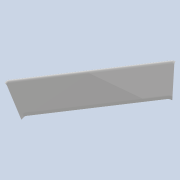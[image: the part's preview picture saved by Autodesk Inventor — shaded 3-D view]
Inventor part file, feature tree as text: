
AUTODESK INVENTOR PART (.ipt)
format: ipt  version: 2020.4 (Build 244396010, 396A)  size: 9,091,584 bytes
history: native  units: in
note: dims shown in document units (in); Inventor stores cm internally (conversion verified against a paired STEP export)
features: other x165, extrude x70, fillet x51, projected_geometry x6, sketch x5, move_body x5, hole x4, loft x3, plane x3, reference x2, boolean_combine x1, direct_edit x1, split x1
ambient origin geometry x8: Origin, YZ Plane, XZ Plane, XY Plane, X Axis, Y Axis, Z Axis, Center Point
bodies: Body (feature_tree), BodyFeature (feature_tree), BodyCut (feature_tree), BodyCutFeature (feature_tree), BodyCutFilletFeature (feature_tree), BodyCutCombineFeature (feature_tree), BodyCutEdgeFilletFeature (feature_tree), BodyRibFrontFilletsFeature (feature_tree), BodyBackRibFilletsFeature (feature_tree), BodyFretboardFilletsFeature (feature_tree), BodyFrontTopFilletsFeature (feature_tree), BodyFrontBottomFilletsFeature (feature_tree), BodyFrontNeckFilletsFeature (feature_tree), Solid22 (feature_tree), Solid23 (feature_tree), Solid62 (feature_tree), Solid64 (feature_tree), Solid65 (feature_tree), Solid68 (feature_tree), Solid50 (feature_tree), Solid52 (feature_tree), Solid54 (feature_tree), Solid56 (feature_tree), Solid57 (feature_tree), Solid59 (feature_tree)
feature tree (317):
  other  "MainBody"
  extrude  "NeckMountsProfileFeature"  Depth=0.5in TaperAngle=0.0deg
  other  "NeckPlane"
  extrude  "8StringFeature"  Depth=0.25in
  extrude  "6StringFeature"  Depth=0.25in
  extrude  "HornFeature"  Depth=0.25in
  other  "6StringNeckFeature"
  other  "8StringNeckFeature"
  fillet  "InsideCornerFilletsFeature1/8"  Radius=0.6788in
  fillet  "OutsideFilletsFeature1/2"  Radius=0.125in
  fillet  "NeckMountOutsideFilletsFeature1/4"  Radius=0.5in
  fillet  "TipFilletsFeature1/8"  Radius=0.125in
  fillet  "BottomHornTipFilletFeature1/10"  Radius=0.1in
  fillet  "BottomHornFilletsFeature1/8"  Radius=0.125in
  fillet  "InsideHandleFilletsFeature1/2"  Radius=0.5in
  fillet  "InsideHandleFilletsFeature1/8"  Radius=0.125in
  fillet  "InsideTopHornFilletsFeature1/4"  Radius=0.25in
  fillet  "InsideTopHornFilletsFeature1/2"  Radius=0.5in
  fillet  "InsideBottomHornFilletsFeature1/4"  Radius=0.25in
  other  "PickupsOriginal"
  other  "MiddlePlane"
  other  "PickupsCustom"
  other  "PickupsModified"
  extrude  "TopPickupsIndentFeature"  Depth=0.25in
  extrude  "BottomPickupsIndentFeature"  Depth=0.25in
  extrude  "TopPickupHolesFeature"  Depth=0.25in
  extrude  "BottomPickupHolesFeature"  Depth=0.25in
  fillet  "PickupIndentFilletsFeature"  Radius=1.1649in
  other  "Frets"
  other  "FretsPreview"
  other  "TopHornHandleIndent"
  extrude  "TopHornBodyHandleFeature"  Depth=0.25in
  extrude  "TopHornHornHandleFeature"  Depth=0.25in
  other  "HornSculptFeature"
  other  "TopHornHandleFront"
  extrude  "TopHornHandleFrontFeature"  Depth=0.25in
  extrude  "TopHornHandleFront2Feature"  Depth=0.25in
  extrude  "TopHornHandleFront3Feature"  TaperAngle=45.0deg  [1 undecoded]
  other  "TopHornHandleBack"
  extrude  "TopHornHandleBackFeature"  TaperAngle=120.0deg  [1 undecoded]
  extrude  "TopHornHandleBack2Feature"  Depth=0.25in
  extrude  "TopHandleFeature"  Depth=0.25in
  extrude  "TopHandleFrontFeature"  Depth=0.25in
  extrude  "TopHandleBackFeature"  Depth=0.25in
  other  "Tuners"
  hole  "TunerHolesFeature"  [1 undecoded]
  other  "LogoMount"
  extrude  "LogoMountFeature"  Depth=0.25in
  other  "SideProfile"
  extrude  "SideProfileFeature"  Depth=0.25in
  other  "KeyboardCompartmentSidePlane"
  extrude  "KeyboardCompartmentFeature"  Depth=0.25in
  fillet  "KeyboardCompartmentFilletsFeature"  Radius=0.101in
  other  "ControlsBottom"
  other  "ControlsTop2"
  other  "ControlsTop1"
  extrude  "ControlsTop1Feature"  Depth=0.25in
  extrude  "ControlsTop2Feature"  Depth=0.25in
  extrude  "ControlsBottomFeature"  Depth=0.25in
  other  "HornSculptSideProfileFeature"
  fillet  "HornFretboardFilletFeature"  Radius=0.933in
  other  "ElectronicsCompartments"
  other  "InsideFacePlane1"
  other  "InsideFacePlane2"
  other  "InsideFacePlane3"
  extrude  "ElectronicCompartmentTopFeature"  Depth=0.25in
  extrude  "ElectronicCompartmentBottomFeature"  Depth=0.25in
  other  "ElectronicCompartmentsSculpt1Feature"
  other  "ElectronicCompartmentsSculpt2Feature"
  other  "ElectronicCompartmentsSculpt3Feature"
  other  "ElectronicCompartmentsSubtractFeature"
  extrude  "ElectronicCompartmentsSubtract2Feature"  Depth=0.25in
  fillet  "ElectronicCompartmentFillets1Feature"  Radius=3.5in
  fillet  "ElectronicCompartmentFillets2Feature"  Radius=1.277in
  extrude  "ControlIndentsBottomFeature"  Depth=0.25in
  fillet  "ElectronicCompartmentFillets3Feature"  Radius=1.5in
  fillet  "ElectronicCompartmentFillets4Feature"  Radius=1.0857in
  extrude  "ControlIndentsTopFeature"  Depth=0.25in
  other  "ControlIndents2Top"
  extrude  "ControlIndents2TopFeature"  Depth=0.25in
  fillet  "ControlIndents3FilletsFeature"  Radius=4.5in
  extrude  "ControlIndents2RecutFeature"  Depth=0.25in
  fillet  "ElectronicCompartmentInsideFilletsFeature"  Radius=0.1512in
  other  "BottomBridgePickupWirePlane"
  extrude  "BottomBridgePickupWireHoleFeature"  Depth=0.25in
  other  "BottomNeckPickupWirePlane"
  extrude  "BottomNeckPickupWireFeature"  Depth=0.25in
  extrude  "TopPickupWireFeature"  Depth=0.25in
  other  "SeaboardBlockCircuitboardMounts"
  extrude  "SeaboardBlockMountStemFeature"  Depth=0.25in
  extrude  "SeaboardBlockMountsFeature"  Depth=0.25in
  other  "SeaboardBlockKeyMounts"
  extrude  "SeaboardBlockKeyMountsFeature"  Depth=0.25in
  extrude  "SeaboardBlockRibbonsFeature"  Depth=0.25in
  extrude  "TunersTopFeature"  Depth=0.25in
  extrude  "TunersMiddleFeature"  Depth=0.25in
  extrude  "TunersBottomFeature"  Depth=0.25in
  fillet  "TunerFilletsFeature"  Radius=1.1386in
  extrude  "NeckCutFeature"  Depth=0.25in
  fillet  "NeckCutFilletFeature"  Radius=4.009in
  other  "NeckCutCombineFeature"
  fillet  "NeckCutEdgeFilletFeature"  Radius=1.481in
  fillet  "NeckCutCornerFilletsFeature"  Radius=0.25in
  extrude  "NeckMountsFeature"  Depth=0.25in
  extrude  "FretMarkersTopFeature"  Depth=0.25in
  extrude  "FretMarkersBottomFeature"  Depth=0.25in
  extrude  "FretsPreviewFeature"  TaperAngle=0.0deg  [1 undecoded]
  extrude  "FretLocksPreviewFeature"  Depth=0.3937in
  hole  "FretLocksHolesFeature"  [1 undecoded]
  extrude  "TopHornHandleBodyFeature"  Depth=0.25in
  other  "TopHornSculpt3Feature"
  other  "TopHornSculpt4Feature"
  other  "TopHornSculpt5Feature"
  fillet  "TopHornHandleBodyFilletsFeature"  Radius=0.9256in
  fillet  "TopHornHandleFilletsFeature"  [1 undecoded]
  other  "TopHornAdjustFeature"
  fillet  "TopHornAdjustFilletFeature"  [1 undecoded]
  other  "HandlePlane1"
  other  "HandlePlane2"
  other  "Handle"
  extrude  "HandleBackFeature"  Depth=0.25in
  extrude  "HandleFrontFeature"  Depth=0.25in
  other  "HandleSculpt1Feature"
  other  "HandleSculpt2Feature"
  other  "HandleSculpt3Feature"
  other  "HandleSculpt4Feature"
  other  "HandleSculpt5Feature"
  other  "HandleSculpt6Feature"
  other  "HandleEdit1Feature"
  other  "HandleEdit2Feature"
  fillet  "HandleBodyFilletsFeature"  Radius=25.5in
  fillet  "HandleRibFilletsFeature"  Radius=0.3333in
  other  "HornBackSculptFeature"
  other  "HornHandleBackSculpt1Feature"
  other  "HornHandleBackSculpt2Feature"
  fillet  "HornHandleackSculptFilletsFeature"  Radius=0.333in
  fillet  "HandleMeshFilletsFeature"  Radius=0.1in
  fillet  "HornMeshFillets1Feature"  Radius=0.1in
  fillet  "FretboardEndFilletsFeature"  [1 undecoded]
  other  "KeyboardCompartmentSideProfile"
  extrude  "KeyboardCompartmentExactFeature"  Depth=0.25in
  extrude  "KeyboardCompartmentSideFeature"  Depth=0.25in
  other  "KeyboardCompartmentExactSubtractFeature"
  other  "8NeckSplitFeature"
  other  "8NeckLoftStartPlane"
  other  "8NeckLoftEndPlane"
  loft  "8NeckLoftFeature"
  other  "6NeckSplitForLoftFeature"
  other  "6NeckLoftEndPlane"
  other  "6NeckLoftStartPlane"
  extrude  "OscScreenFeature"  TaperAngle=0.0deg  [1 undecoded]
  other  "OscCompartmentPlane"
  other  "OscIndentPlane"
  extrude  "OscCompartmentFeature"  Depth=0.25in
  other  "OscCompartmentSubtractFeature"
  extrude  "OscMountFeature"  Depth=0.25in
  other  "OscCoverIndentPlane"
  extrude  "OscCoverIndentFeature"  Depth=0.25in
  fillet  "OscCoverIndentFilletsFeature"  [1 undecoded]
  extrude  "OscCoverMountHolesFeature"  Depth=0.25in TaperAngle=0.0deg
  fillet  "ElectronicCompartmentLastFilletFeature"  Radius=0.3in
  loft  "6NeckLoftFeature"
  extrude  "6CloseCutFeature"  Depth=0.25in
  other  "HeadSculpt1Feature"
  other  "HeadThickness"
  other  "HeadSculpt2Feature"
  other  "HeadSculpt3Plane"
  extrude  "HeadSculpt3Feature"  Depth=0.25in
  other  "HeadSculpt4Feature"
  other  "8HeadCombineFeature"
  other  "8HeadCleanupFeature"
  fillet  "8HeadFilletFeature"  Radius=0.333in
  other  "HeadSculpt5Plane"
  other  "HeadSculpt5Feature"
  other  "HeadSculpt6Feature"
  other  "HeadSculpt7Plane"
  extrude  "HeadSculpt7Feature"  Depth=0.25in
  other  "6StringCombineFeature"
  other  "6NeckFilletSplitFeature"
  other  "8NeckFilletSplitFeature"
  fillet  "InsideHeadFilletFeature"  Radius=0.125in
  other  "CombineFilletsFeature"
  fillet  "HornHeadFilletsFeature"  Radius=0.5in
  fillet  "HornFillet3Feature"  Radius=5.55in
  other  "HornFinalSplitFeature"
  other  "6FinalSplitFeature"
  other  "6CombineFeature"
  other  "8NeckJoin"
  other  "6NeckJoin"
  extrude  "8NeckJoinFeature"  Depth=0.25in
  fillet  "8NeckJoinFilletFeature"  Radius=0.2in
  extrude  "6NeckJoinFeature"  Depth=0.25in
  extrude  "SeaboardBlockMountHolesFeature"  TaperAngle=0.0deg  [1 undecoded]
  extrude  "PickupRecutFeature"  Depth=0.25in
  extrude  "BackCoverIndentFeature"  Depth=0.3937in
  extrude  "ElectronicsCompartmentSupportFeature"  Depth=0.25in
  fillet  "ElectronicsCompartmentSupportFilletsFeature"  Radius=1.125in
  hole  "BackCoverMountsFeature"  [1 undecoded]
  other  "OscCoverBottom"
  other  "OscCoverTopPlane"
  other  "OscCoverMounts"
  loft  "OscCoverFeature"
  extrude  "OscCoverBodyCutFeature"  Depth=0.05in TaperAngle=0.0deg
  fillet  "OscCoverBodyCutFilletsFeature"  Radius=0.05in
  other  "OscCoverBodyCutSubtractFeature"
  fillet  "OscCoverBodyFilletFeature"  Radius=0.125in
  extrude  "OscCoverMountsFeature"  Depth=0.25in
  other  "LogoCompartment"
  extrude  "LogoCompartmentFeature"  Depth=0.25in
  extrude  "LogoCompartmentMountsFeature"  Depth=0.25in
  fillet  "LogoCompartmentFillet1Feature"  Radius=0.5in
  fillet  "LogoCompartmentFillet2Feature"  Radius=0.25in
  fillet  "LogoCompartmentFillet3Feature"  Radius=0.1in
  fillet  "LogoCompartmentFillet4Feature"  Radius=0.13in
  fillet  "LogoCompartmentFillet5Feature"  Radius=3.063in
  fillet  "LogoCompartmentFillet6Feature"  Radius=0.1295in
  fillet  "LogoCompartmentFillet7Feature"  Radius=0.1295in
  fillet  "LogoCompartmentFillet8Feature"  Radius=0.5708in
  hole  "LogoCompartmentHolesFeature"  [1 undecoded]
  boolean_combine  "Combine26"
  direct_edit  "Direct Edit19"
  plane  "Work Plane98"
  plane  "Work Plane97"
  split  "Split16"
  other  "KeyboardCompartment"
  other  "TopHandle"
  other  "TunerLocksBody"
  other  "FretsBody"
  other  "TunersTop"
  other  "TunersMiddle"
  other  "TunersBottom"
  other  "ElectronicCompartments1Body"
  other  "NeckCut"
  other  "NeckMounts"
  other  "TopHornHandle"
  other  "TopHornHandleBody"
  projected_geometry  "Projected Loop22"
  projected_geometry  "Projected Loop23"
  other  "TopHandleFront"
  projected_geometry  "Projected Loop24"
  other  "TopHandleBack"
  other  "HandleBody"
  other  "TopHornSculpt3Plane"
  other  "TopHornSculpt4Plane"
  other  "TopHornSculpt5Plane"
  other  "HandleSculpt1Plane"
  other  "HandleSculpt2Plane"
  other  "HandleSculpt3Plane"
  other  "HandleSculpt4Plane"
  other  "HandleSculpt5Plane"
  other  "HandleSculpt6Plane"
  other  "HornBody"
  other  "8StringBody"
  other  "6StringBody"
  other  "NeckMountsProfile"
  other  "HornBackSculptPlane"
  other  "HornSculptFrontPlane"
  plane  "Work Plane62"
  other  "8NeckStartProfile"
  other  "8NeckEndProfile"
  sketch  "Sketch127"  dims[d8=0.7696in d18=0.5in d119=1.75in d120=0.0in]
  other  "6NeckLoftStartProfile"
  other  "6NeckLoftEndProfile"
  projected_geometry  "Projected Loop27"
  other  "6CloseCut"
  sketch  "Sketch131"  dims[d433=1.0857in d464=4.5in d466=0.25in]
  other  "HeadSculpt1Plane"
  other  "HeadSculpt2Plane"
  other  "HeadSculpt3Profile"
  other  "HeadSculpt4Plane"
  other  "HeadSculpt7Profile"
  other  "6NeckFilletSplit"
  other  "8NeckFilletSplit"
  sketch  "Sketch138"  dims[d501=0.25in d582=1.12in]
  sketch  "Sketch139"  dims[d644=25.0in d654=0.6788in d681=0.6788in d700=0.125in d702=0.5in d703=0.125in d705=0.1in d706=0.125in d707=0.5in d708=0.125in d709=0.25in d710=0.5in d711=0.25in]
  other  "ControlIndentsBottom"
  other  "BottomBridgePickupWireHole"
  other  "BottomNeckPickupWire"
  other  "TopPickupWire"
  other  "HornHandleBackSculpt1Plane"
  other  "HornHandleBackSculpt2Plane"
  sketch  "Sketch165"  dims[d716=2.2835in d717=0.0515in d718=13.825in d719=0.213in d721=0.9414in d722=1.1649in d724=5.7in d725=7.5379in d726=0.2542in d727=2.0in d728=45.0deg d729=120.0deg d730=0.3642in d731=0.9371in d745=5.6289in d747=6.0in d748=4.3in d750=0.8658in d751=0.6506in d753=0.4054in d754=0.8in d779=0.101in d781=1.7in d782=7.125in d783=2.6in d784=0.933in d787=1.1in d792=3.625in d793=4.0in d819=3.5in d825=1.277in d834=1.277in d836=1.5in d837=1.0857in d838=3.0in d839=2.0in d841=4.5in d846=3.3665in d850=0.1512in d853=2.6in d864=1.5757in d961=0.5in d962=0.5in d963=0.3779in d964=0.3779in d965=0.45in d966=0.45in d967=0.8795in d968=1.1386in d969=1.1386in d970=0.45in d971=4.009in d972=1.481in d979=0.25in d980=0.25in d982=0.1718in d983=0.1718in d984=0.0in d985=0.7874in d987=4.0in d988=0.3937in d990=1.0in d994=2.746in d995=1.481in d996=0.9256in d999=0.0in d1000=0.0in d1022=26.75in d1023=28.0in d1024=25.5in d1026=0.3333in d1041=0.333in d1042=0.1in d1044=0.1in d1048=0.0in d1049=0.0in d1054=0.1in d1055=0.1in d1057=0.748in d1060=0.0in d1061=0.0in d1064=0.4662in d1092=0.7in d1095=1.7in d1100=0.0in d1101=0.0in d1117=0.25in d1118=0.0in d1119=0.3in d1120=0.0in d1122=0.2in d1123=0.0in d1277=0.6459in d1329=0.5333in d1334=0.333in d1335=0.5333in d1339=0.125in d1348=0.5in d1358=5.55in d1359=1.75in d1373=0.2in d1375=0.1in d1376=0.0in d1406=1.125in d1430=3.1496in d1432=0.525in d1433=0.3937in d1435=1.0in d1439=1.8in d1440=1.125in d1441=0.2in d1475=0.1in d1476=0.75in d1477=0.375in d1478=0.25in d1479=0.5635in d1480=0.5in d1481=0.8108in d1483=0.05in d1484=0.0in d1485=0.05in d1486=0.0in d1487=0.05in d1488=0.0in d1489=0.125in d1490=0.1in d1491=2.846in d1492=1.481in d1493=0.5in d1494=0.25in d1496=0.1in d1504=0.13in d1508=0.1in d1511=3.063in d1512=0.1295in d1513=0.1295in d1526=0.5708in d1527=0.1286in d1528=1.3799in d1529=1.3958in d1530=1.1055in d1531=0.8208in d1534=2.3622in d1536=0.45in d1537=0.3937in d1539=1.0in d1574=1.0in d1575=0.0in d1576=0.0in d1577=0.4789in d1578=0.4308in d1579=1.1471in d1580=2.5in d1581=1.275in d1582=1.1845in d1583=1.481in d1584=1.1384in d1585=0.7644in d1586=2.746in d1587=0.264in d1588=0.4in d1589=0.0in d1590=0.75in d1591=0.0in d1592=1.0in d1593=0.0in d1594=1.0in d1595=0.0in d1596=0.144in d1597=3.75in d1598=0.1295in d1599=0.1295in d1638=10.0in d1639=14.2465in d1641=11.25in d1648=0.5in d1649=0.0in d1650=28.0in d1657=1.0in d1659=5.5in d1660=4.25in d1662=0.3333in d1663=0.0in d1664=10.0in d1665=1.0in d1671=0.1in d1672=0.5in d1676=3.0in d1677=2.425in d1682=0.75in d1683=0.0in d1690=1.1878in d1691=0.9817in d1692=1.0844in d1693=0.8784in d1695=0.2in d1696=0.0in d1750=1.525in d1751=0.0in d1752=0.5in d1777=0.5in d1778=0.0in d1779=0.5in d1780=0.0in d1781=0.5in d1782=0.0in d1783=0.6in d1784=0.0in d1790=0.65in d1791=0.0in d1792=0.65in d1793=0.0in d1795=0.125in d1821=0.1in d1828=0.0in d1829=0.0in d1830=0.475in d1831=0.125in d1832=0.125in d1843=3.0403in d1844=2.1333in d1845=0.758in d1847=1.75in d1848=0.0in d1849=1.9in d1850=0.0in d1851=1.9in d1852=0.0in d1858=0.9in d1859=0.0in d1862=0.0in d1863=0.0in d1864=0.5in d1865=0.0in d1866=0.5in d1867=0.0in d1870=0.2056in d1871=0.257in d1872=0.0674in d1875=0.25in d1876=0.0in d1877=0.15in d1880=0.15in d1882=0.05in d1883=0.05in d1885=1.3537in d1887=10.0in d1888=0.1in d1889=0.1in d1890=20.0in d1891=20.0in d1894=0.0618in d1900=0.1in d1901=0.4524in d1903=0.006in d1904=0.0in d1915=0.22in d1921=0.0in d1922=90.0deg d1923=0.0in d1924=90.0deg d1925=1.2in d1926=0.7in d1927=0.3333in d1928=0.001in d1929=0.25in d1930=1.25in d1931=0.25in d1935=0.8in d1936=0.3489in d1937=0.22in d1938=0.25in d1939=0.5in d1940=0.6in d1941=0.15in d1942=0.4in d1943=0.0in d1944=90.0deg d1945=0.0in d1946=90.0deg d1948=1.3333in d1949=2.125in d1951=1.125in d1952=2.55in d1957=3.0in d1958=0.1in d1959=0.1in d1960=0.1in d1961=1.0in d1962=0.0in d1966=1.0in d1967=0.0in d1968=0.44in d1969=0.0in d1975=0.1in d1976=0.1in d1980=10.6875in d1981=5.1875in d1982=0.85in d1983=0.3333in d1985=7.5816in d1987=0.1in d1988=0.0in d1989=0.1875in d1990=0.5333in d1992=150.0deg d1993=3.25in d1996=-0.325in d1997=-0.125in d1998=1.0in d1999=0.0in d2004=0.5in d2005=0.0in d2007=0.0938in d2008=0.5in d2009=0.25in d2010=2.3125in d2011=0.7188in d2015=0.25in d2016=5.0in d2019=0.125in d2020=0.25in d2027=0.2in d2028=0.0in d2029=0.02in d2030=0.0in d2039=0.55in d2047=0.25in d2048=0.25in d2049=0.0in d2050=0.0in d2052=2.295in d2053=0.0in d2056=0.25in d2058=0.25in d2059=0.3333in d2060=0.3333in d2061=0.25in d2062=0.3333in d2063=0.3333in d2064=0.0in d2065=0.0in d2066=0.339in d2067=0.1643in d2068=0.1in d2069=0.1in d2070=0.1in d2071=0.1in d2072=0.1643in d2073=0.1643in d2074=0.1643in d2077=3.3125in d2078=3.313in d2079=0.305in d2080=0.3333in d2081=1.0in d2082=0.0in d2083=0.3333in d2084=0.0in d2086=0.719in d2087=2.3125in d2088=0.125in d2089=0.1in d2090=0.438in d2091=0.438in d2092=0.438in d2093=0.438in d2094=0.25in d2095=0.0in d2096=0.25in d2097=0.25in d2098=2.0in d2100=2.5in d2102=0.75in d2103=0.25in d2104=0.25in d2105=0.0in d2106=0.625in d2111=10.0in d2112=0.125in d2113=0.3333in d2117=1.75in d2118=1.25in d2119=1.625in d2120=0.25in d2121=1.0in d2122=0.1in d2125=0.7in d2132=1.625in d2133=1.0in d2134=0.1in d2135=1.0in d2136=1.0in d2137=0.1in d2138=1.025in d2139=1.025in d2140=0.5in d2141=0.7in d2142=1.075in d2143=0.7in d2144=0.5in d2146=0.25in d2147=0.25in d2148=0.5in d2149=1.75in d2150=0.0in d2151=0.0in d2152=0.035in d2153=0.0in d2154=0.0in d2155=0.0in d2156=-0.325in d2157=1.0in d2158=0.2in d2159=0.0in d2160=1.0in d2161=0.2in d2162=0.0in d2164=1.0in d2165=2.2612in d2166=0.605in d2167=0.01in d2168=0.3333in d2169=0.5388in d2170=0.4in d2171=2.625in d2172=1.375in d2173=0.172in d2174=0.281in d2175=0.5in d2176=0.0in d2177=-2.0in d2178=1.797in d2179=0.0in d2180=-0.125in d2181=0.06in d2182=0.06in d2183=0.505in d2184=0.9375in d2185=2.625in d2186=1.375in d2187=2.5in d2188=1.0313in d2189=0.05in d2190=0.1719in d2191=0.0625in d2192=0.0625in d2193=0.1094in d2194=0.0312in d2195=0.0312in d2196=0.0312in d2197=0.0312in d2198=0.0312in d2199=0.0312in d2200=0.0312in d2201=0.0312in d2202=0.203in d2203=0.0in d2207=-0.2in d2211=0.15in d2212=1.0in d2213=0.0in d2214=0.15in d2215=0.15in d2216=0.1in d2220=0.05in d2221=1.5in d2222=0.0in d2230=0.6836in d2238=1.0in d2239=0.25in d2240=0.1in d2241=0.0689in d2243=1.1408in d2244=0.449in d2245=1.6223in d2246=2.1038in d2247=0.449in d2248=0.0463in d2249=0.4549in d2251=0.3908in d2252=0.3908in d2255=0.8in d2257=3.5in d2259=1.1973in d2261=0.625in d2262=0.625in d2263=0.536in d2264=2.7in d2265=0.25in d2266=0.2in d2267=0.0in d2268=0.2in d2269=0.0in d2278=0.4264in d2279=1.0in d2280=0.0in d2281=21.986in d2282=0.0in d2283=0.1in d2284=0.1in d2285=0.5in d2286=0.0in d2287=0.5333in d2288=0.1in d2293=0.85in d2294=1.0in d2295=0.25in d2296=0.749in d2297=0.0in d2298=0.25in d2299=0.1984in d2300=0.1in d2301=0.0in d2302=0.2in d2303=0.0in d2304=0.481in d2305=0.481in d2306=0.5in d2307=0.25in d2308=0.1in d2309=0.75in d2310=0.375in d2311=0.25in d2312=0.5635in d2313=0.5in d2314=0.8108in d2319=0.0in d2320=0.0in d2321=90.0deg d2322=0.0in d2323=90.0deg d2324=0.5in d2325=0.0in d2326=28.0in d2327=1.0in d2328=1.5in d2329=0.0in d2330=0.2in d2331=0.2in d2333=0.22in d2335=0.12in d2336=0.12in d2337=0.1in d2338=0.1in d2339=0.75in d2340=0.375in d2341=0.25in d2342=0.5635in d2343=0.5in d2344=0.8108in d2347=0.25in d2348=0.3in d2349=0.15in d2350=0.15in d2351=0.3in d2352=0.15in d2353=0.3in d2354=0.25in d2355=0.25in d2356=0.25in d2357=0.25in d2358=0.25in d2359=0.1958in d2360=0.1958in d2365=0.2in d2366=0.0in d2381=0.7in d2382=0.6in d2387=0.089in d2408=0.3333in d2409=0.0in d2410=0.031in d2412=0.106in d2413=0.072in d2414=0.033in d2415=0.125in d2416=0.132in d2417=0.101in d2418=0.074in d2419=0.05in d2420=0.75in d2421=0.375in d2422=0.25in d2423=0.5635in d2424=0.5in d2425=0.8108in d2428=0.0in d2429=0.0in d2430=-0.0394in d2431=0.0in d2432=0.0in d2433=-0.0394in d2434=0.0in d2435=0.0in d2436=-0.0394in d2437=0.0in d2438=0.0in d2439=-0.0394in d620=0.5in d621=0.0344in d622=0.5in d623=0.0344in d1625=0.5in d1626=0.0344in d1627=0.5in d1628=0.0344in d1730=0.5in d1731=0.0344in d1732=0.5in d1733=0.0344in d1822=0.5in d1823=0.0344in d1824=0.5in d1825=0.0344in d1837=0.5in d1838=0.0344in d1839=0.5in d1840=0.0344in d1860=0.5in d1861=0.0344in d1947=0.5in d1950=0.0344in d2012=0.5in d2013=0.0344in d2101=0.5in d2392=0.5in d2393=0.0344in d2394=0.5in d2395=0.0344in]
  other  "OscScreen"
  other  "OscCompartment"
  other  "OscMount"
  other  "OscCoverPlane"
  other  "OscCoverIndent"
  other  "OscCoverMountHoles"
  projected_geometry  "Projected Loop32"
  other  "KeyboardCompartmentExact"
  projected_geometry  "Projected Loop35"
  other  "SeaboardBlockMountHoles"
  reference  "Reference6"
  reference  "Reference7"
  other  "PickupRecut"
  other  "BackCoverIndent"
  other  "ElectronicsCompartmentSupport"
  other  "BackCoverMounts"
  other  "OscCoverTop"
  other  "OscCoverBody"
  other  "Delete13"
  move_body  "Move3"
  other  "Delete14"
  other  "6StringNeckCombineBody"
  other  "8StringNeckBody"
  other  "6StringNeckBody"
  other  "TopHornBody"
  other  "8StringCombinedBody"
  other  "6StringCombinedBody"
  other  "Delete18"
  other  "<userpath>\Desktop\switchback\src\switchback-exploded.iam"
  other  "switchback-exploded.iam"
  other  "seaboard-block-keyboard:1"
  move_body  "Move4"
  move_body  "Move5"
  move_body  "Move6"
  move_body  "Move7"
note: 13 required parameter values undecoded (feature->parameter linkage not recoverable at this tier; creation-order binding heuristic only, values carry confidence <= 0.55)
